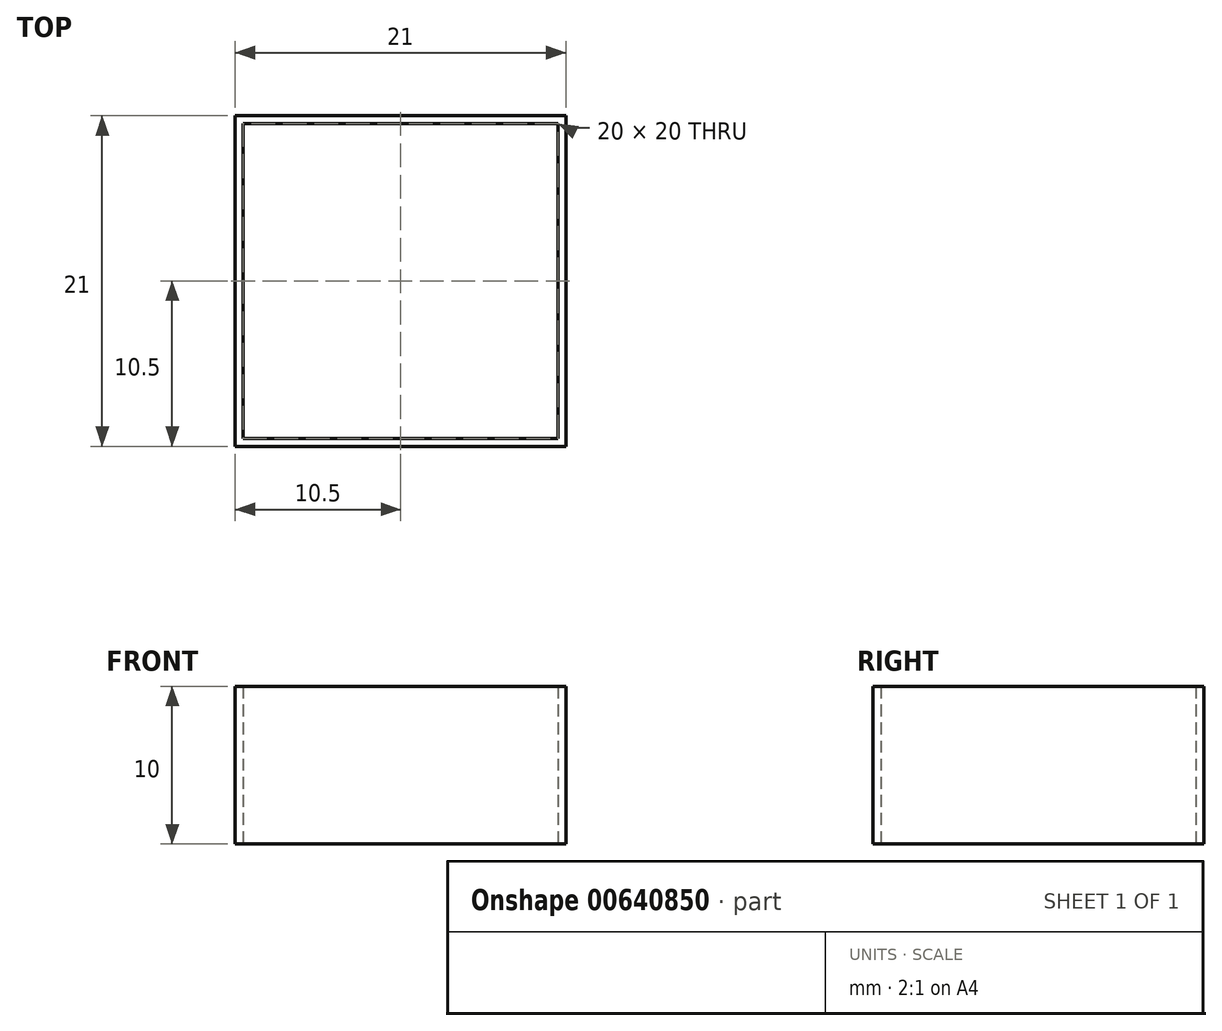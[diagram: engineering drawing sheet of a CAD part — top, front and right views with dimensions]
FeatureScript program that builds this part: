
annotation { "Feature Type Name" : "Feature", "Feature Type Description" : "" }
export const myFeature = defineFeature(function(context is Context, id is Id, definition is map)
    precondition{}
    {
        {
            var Q0;
            Q0=qCreatedBy(makeId("Top.planeOp"),FACE);
            var sketch = newSketch(context, id + "F0", { "sketchPlane" : qUnion([Q0])});
            skLineSegment(sketch, "E0.bottom", {"start": v(-10, 10) * mm, "end": v(10, 10) * mm});
            skLineSegment(sketch, "E0.top", {"start": v(-10, -10) * mm, "end": v(10, -10) * mm});
            skLineSegment(sketch, "E0.left", {"start": v(-10, 10) * mm, "end": v(-10, -10) * mm});
            skLineSegment(sketch, "E0.right", {"start": v(10, 10) * mm, "end": v(10, -10) * mm});
            skPoint(sketch, "E0.middle", {"position": v(0, 0) * mm});
            skLineSegment(sketch, "E1.bottom", {"start": v(-10.5, 10.5) * mm, "end": v(10.5, 10.5) * mm});
            skLineSegment(sketch, "E1.top", {"start": v(-10.5, -10.5) * mm, "end": v(10.5, -10.5) * mm});
            skLineSegment(sketch, "E1.left", {"start": v(-10.5, 10.5) * mm, "end": v(-10.5, -10.5) * mm});
            skLineSegment(sketch, "E1.right", {"start": v(10.5, 10.5) * mm, "end": v(10.5, -10.5) * mm});
            skSolve(sketch);
        }
        {
            var Q0;
            Q0=makeQuery(id+"F0.imprint","IMPRINT",FACE,{"disambiguationData":[TD([[makeQuery(id+"F0.imprint","IMPRINT",EDGE,{"derivedFrom":sQuery(id+"F0.wireOp",EDGE,"E0.bottom")}),1.0]])]});
            extrude(context, id + "F1", {"entities" : qUnion([Q0]), "depth" : 10 * mm, "offsetDistance" : 25 * mm});
        }
    });
